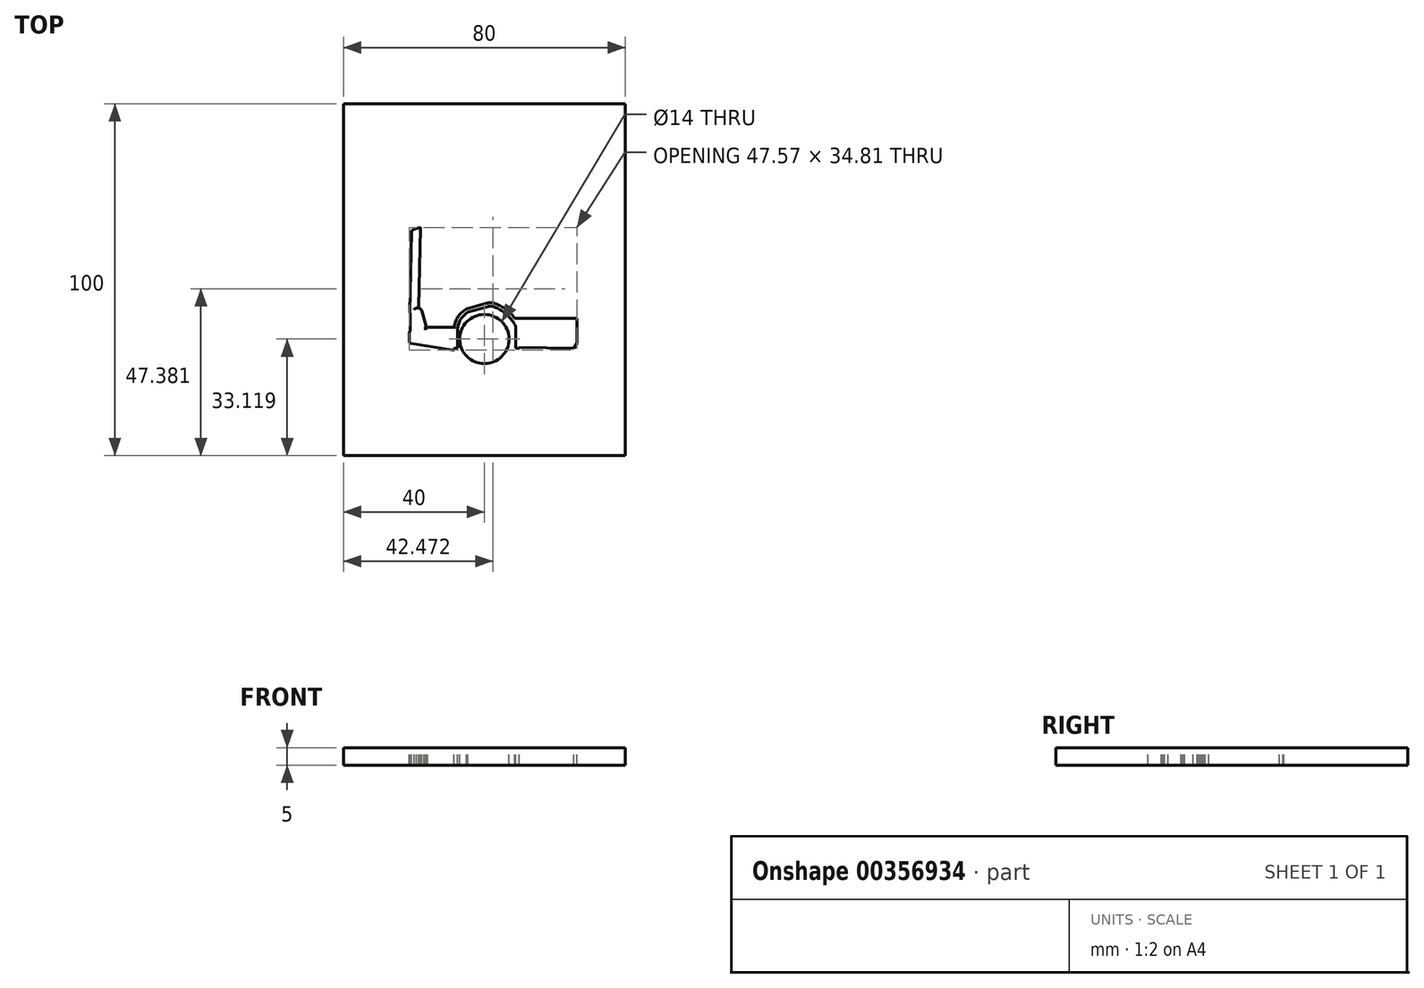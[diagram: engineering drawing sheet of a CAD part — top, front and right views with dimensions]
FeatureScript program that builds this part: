
annotation { "Feature Type Name" : "Feature", "Feature Type Description" : "" }
export const myFeature = defineFeature(function(context is Context, id is Id, definition is map)
    precondition{}
    {
        {
            var Q0;
            Q0=qCreatedBy(makeId("Top.planeOp"),FACE);
            var sketch = newSketch(context, id + "F0", { "sketchPlane" : qUnion([Q0])});
            skLineSegment(sketch, "E0.bottom", {"start": v(40, -50) * mm, "end": v(-40, -50) * mm});
            skLineSegment(sketch, "E0.top", {"start": v(40, 50) * mm, "end": v(-40, 50) * mm});
            skLineSegment(sketch, "E0.left", {"start": v(40, -50) * mm, "end": v(40, 50) * mm});
            skLineSegment(sketch, "E0.right", {"start": v(-40, -50) * mm, "end": v(-40, 50) * mm});
            skPoint(sketch, "E0.middle", {"position": v(0, 0) * mm});
            skCircle(sketch, "E1", {"center": v(0, -16.88) * mm, "radius": 7 * mm});
            skCircle(sketch, "E2", {"center": v(0, -16.88) * mm, "radius": 3.75 * mm});
            skCircle(sketch, "E3", {"center": v(0, -16.88) * mm, "radius": 1.5 * mm});
            skCircle(sketch, "E4", {"center": v(0, -16.88) * mm, "radius": 0.75 * mm});
            skLineSegment(sketch, "E5", {"start": v(-7.57, -19.52) * mm, "end": v(-7.57, -14.2) * mm});
            skArc(sketch, "E6", {"start": v(-7.57, -14.2) * mm, "mid": v(-6.8, -11.34) * mm, "end": v(-4.68, -9.26) * mm});
            skLineSegment(sketch, "E7", {"start": v(-4.68, -9.26) * mm, "end": v(0.98, -7.65) * mm});
            skArc(sketch, "E8", {"start": v(0.98, -7.65) * mm, "mid": v(1.86, -7.55) * mm, "end": v(2.72, -7.73) * mm});
            skPoint(sketch, "E9.end.orphan", {"position": v(7.1, -19.52) * mm});
            skArc(sketch, "E10", {"start": v(2.72, -7.73) * mm, "mid": v(6.11, -9.74) * mm, "end": v(8.64, -12.76) * mm});
            skPoint(sketch, "E11.end.orphan", {"position": v(7.3, -19.52) * mm});
            skArc(sketch, "E12", {"start": v(8.64, -12.76) * mm, "mid": v(8.84, -13.2) * mm, "end": v(8.94, -13.66) * mm});
            skLineSegment(sketch, "E13", {"start": v(8.94, -13.66) * mm, "end": v(8.94, -19.52) * mm});
            skLineSegment(sketch, "E14.0", {"start": v(9.94, -13.6) * mm, "end": v(9.94, -19.52) * mm});
            skArc(sketch, "E14.1", {"start": v(9.5, -12.25) * mm, "mid": v(9.8, -12.9) * mm, "end": v(9.94, -13.6) * mm});
            skArc(sketch, "E14.2", {"start": v(3.08, -6.8) * mm, "mid": v(6.76, -8.97) * mm, "end": v(9.5, -12.25) * mm});
            skLineSegment(sketch, "E14.3", {"start": v(-8.57, -19.52) * mm, "end": v(-8.57, -14.2) * mm});
            skArc(sketch, "E14.4", {"start": v(-8.57, -14.2) * mm, "mid": v(-7.63, -10.78) * mm, "end": v(-5.07, -8.33) * mm});
            skLineSegment(sketch, "E14.5", {"start": v(-5.07, -8.33) * mm, "end": v(0.7, -6.69) * mm});
            skArc(sketch, "E14.6", {"start": v(0.7, -6.69) * mm, "mid": v(1.9, -6.55) * mm, "end": v(3.08, -6.8) * mm});
            skLineSegment(sketch, "E15", {"start": v(-8.57, -19.52) * mm, "end": v(-7.57, -19.52) * mm});
            skLineSegment(sketch, "E16", {"start": v(8.94, -19.52) * mm, "end": v(9.94, -19.52) * mm});
            skLineSegment(sketch, "E17", {"start": v(9.94, -19.2) * mm, "end": v(25.47, -19.52) * mm});
            skLineSegment(sketch, "E18", {"start": v(25.47, -19.52) * mm, "end": v(26.26, -18.12) * mm});
            skLineSegment(sketch, "E19", {"start": v(26.26, -18.12) * mm, "end": v(9.94, -17.79) * mm});
            skLineSegment(sketch, "E20", {"start": v(26.26, -18.12) * mm, "end": v(26.26, -11.04) * mm});
            skLineSegment(sketch, "E21", {"start": v(26.26, -11.04) * mm, "end": v(8.7, -11.04) * mm});
            skLineSegment(sketch, "E22", {"start": v(9.94, -14.21) * mm, "end": v(26.26, -14.21) * mm});
            skLineSegment(sketch, "E23", {"start": v(11.31, -16.85) * mm, "end": v(11.35, -14.95) * mm});
            skLineSegment(sketch, "E24", {"start": v(11.35, -14.95) * mm, "end": v(15.33, -15.03) * mm});
            skLineSegment(sketch, "E25", {"start": v(15.33, -15.03) * mm, "end": v(15.33, -16.93) * mm});
            skLineSegment(sketch, "E26", {"start": v(15.33, -16.93) * mm, "end": v(11.31, -16.85) * mm});
            skPoint(sketch, "E27.orphan", {"position": v(11.31, -16.93) * mm});
            skLineSegment(sketch, "E28", {"start": v(-8.57, -19.52) * mm, "end": v(-8.57, -20.02) * mm});
            skLineSegment(sketch, "E29", {"start": v(-8.57, -20.02) * mm, "end": v(-8.84, -20.02) * mm});
            skLineSegment(sketch, "E30", {"start": v(-8.96, -20.01) * mm, "end": v(-20.9, -18.07) * mm});
            skLineSegment(sketch, "E31", {"start": v(-21.31, -17.58) * mm, "end": v(-21.31, -17.16) * mm});
            skPoint(sketch, "E32.visualSharp", {"position": v(-21.31, -18) * mm});
            skArc(sketch, "E32.filletArc", {"start": v(-21.31, -17.58) * mm, "mid": v(-21.2, -17.9) * mm, "end": v(-20.9, -18.07) * mm});
            skPoint(sketch, "E33.visualSharp", {"position": v(-8.9, -20.02) * mm});
            skArc(sketch, "E33.filletArc", {"start": v(-8.96, -20.01) * mm, "mid": v(-8.9, -20.02) * mm, "end": v(-8.84, -20.02) * mm});
            skLineSegment(sketch, "E34", {"start": v(-21.31, -17.16) * mm, "end": v(-15.78, -17.16) * mm});
            skLineSegment(sketch, "E35", {"start": v(-15.78, -17.16) * mm, "end": v(-15.37, -17.83) * mm});
            skLineSegment(sketch, "E36", {"start": v(-14.94, -18.07) * mm, "end": v(-8.57, -18.07) * mm});
            skPoint(sketch, "E37.visualSharp", {"position": v(-15.22, -18.07) * mm});
            skArc(sketch, "E37.filletArc", {"start": v(-15.37, -17.83) * mm, "mid": v(-15.18, -18) * mm, "end": v(-14.94, -18.07) * mm});
            skLineSegment(sketch, "E38", {"start": v(-21.31, -17.16) * mm, "end": v(-21.31, -15.3) * mm});
            skArc(sketch, "E39", {"start": v(-21.31, -15.3) * mm, "mid": v(-21.15, -14.65) * mm, "end": v(-20.69, -14.16) * mm});
            skLineSegment(sketch, "E40", {"start": v(-20.6, -14.13) * mm, "end": v(-17.1, -13.91) * mm});
            skLineSegment(sketch, "E41", {"start": v(-16.81, -13.9) * mm, "end": v(-15.78, -17.16) * mm});
            skLineSegment(sketch, "E42", {"start": v(-16.81, -13.9) * mm, "end": v(-8.57, -13.9) * mm});
            skLineSegment(sketch, "E43", {"start": v(-14.97, -13.5) * mm, "end": v(-8.57, -13.5) * mm});
            skLineSegment(sketch, "E44", {"start": v(-8.57, -13.5) * mm, "end": v(-8.57, -13.9) * mm});
            skLineSegment(sketch, "E45", {"start": v(-8.57, -17.7) * mm, "end": v(-14.97, -17.7) * mm});
            skPoint(sketch, "E46.end.orphan", {"position": v(-14.97, -18.07) * mm});
            skLineSegment(sketch, "E47", {"start": v(-14.97, -17.7) * mm, "end": v(-15.22, -17.7) * mm});
            skPoint(sketch, "E48.start.orphan", {"position": v(-14.97, -13.9) * mm});
            skLineSegment(sketch, "E49", {"start": v(-14.97, -13.5) * mm, "end": v(-15.22, -13.5) * mm});
            skLineSegment(sketch, "E50", {"start": v(-15.22, -17.7) * mm, "end": v(-16.11, -14.86) * mm});
            skArc(sketch, "E51", {"start": v(-16.11, -14.86) * mm, "mid": v(-16.09, -14.62) * mm, "end": v(-15.9, -14.48) * mm});
            skLineSegment(sketch, "E52", {"start": v(-15.9, -14.48) * mm, "end": v(-8.57, -14.2) * mm});
            skLineSegment(sketch, "E53", {"start": v(-8.57, -17.3) * mm, "end": v(-15.22, -17.3) * mm});
            skLineSegment(sketch, "E54", {"start": v(-15.22, -17.3) * mm, "end": v(-15.22, -17.7) * mm});
            skPoint(sketch, "E55.visualSharp", {"position": v(-20.64, -14.13) * mm});
            skArc(sketch, "E55.filletArc", {"start": v(-20.6, -14.13) * mm, "mid": v(-20.64, -14.14) * mm, "end": v(-20.69, -14.16) * mm});
            skLineSegment(sketch, "E56", {"start": v(-21.03, -14.46) * mm, "end": v(-21.03, -9.77) * mm});
            skArc(sketch, "E57", {"start": v(-21.03, -9.77) * mm, "mid": v(-20.93, -9.4) * mm, "end": v(-20.66, -9.12) * mm});
            skArc(sketch, "E58", {"start": v(-20.66, -9.12) * mm, "mid": v(-19.78, -8.74) * mm, "end": v(-18.85, -8.55) * mm});
            skArc(sketch, "E59", {"start": v(-18.85, -8.55) * mm, "mid": v(-18.5, -8.66) * mm, "end": v(-18.32, -8.98) * mm});
            skLineSegment(sketch, "E60", {"start": v(-18.32, -8.98) * mm, "end": v(-17.13, -13) * mm});
            skArc(sketch, "E61", {"start": v(-17.13, -13) * mm, "mid": v(-17.16, -13.32) * mm, "end": v(-17.4, -13.53) * mm});
            skLineSegment(sketch, "E62", {"start": v(-17.4, -13.53) * mm, "end": v(-20.6, -13.73) * mm});
            skArc(sketch, "E63", {"start": v(-20.6, -13.73) * mm, "mid": v(-20.85, -13.81) * mm, "end": v(-21.03, -14.01) * mm});
            skArc(sketch, "E64.0", {"start": v(-18.89, -8.05) * mm, "mid": v(-18.18, -8.27) * mm, "end": v(-17.83, -8.92) * mm});
            skArc(sketch, "E65.0", {"start": v(-16.65, -12.86) * mm, "mid": v(-16.66, -13.42) * mm, "end": v(-17, -13.87) * mm});
            skLineSegment(sketch, "E65.1", {"start": v(-17.84, -8.84) * mm, "end": v(-16.65, -12.86) * mm});
            skArc(sketch, "E66.filletArc", {"start": v(-17.1, -13.91) * mm, "mid": v(-17.05, -13.9) * mm, "end": v(-17, -13.87) * mm});
            skLineSegment(sketch, "E67", {"start": v(-16.81, -13.9) * mm, "end": v(-17.1, -13.91) * mm});
            skArc(sketch, "E68", {"start": v(-18.89, -8.05) * mm, "mid": v(-20.08, -8.46) * mm, "end": v(-20.93, -9.4) * mm});
            skLineSegment(sketch, "E69.0", {"start": v(-17.35, -8.76) * mm, "end": v(-16.76, -10.74) * mm});
            skLineSegment(sketch, "E70", {"start": v(-16.76, -10.74) * mm, "end": v(-7.89, -10.74) * mm});
            skArc(sketch, "E71.0", {"start": v(-16.16, -13.5) * mm, "mid": v(-16.24, -13.7) * mm, "end": v(-16.34, -13.9) * mm});
            skArc(sketch, "E72.trimOffspring", {"start": v(-16.7, -14.27) * mm, "mid": v(-16.7, -14.27) * mm, "end": v(-16.7, -14.28) * mm});
            skPoint(sketch, "E73.end.orphan", {"position": v(-15.22, -13.9) * mm});
            skLineSegment(sketch, "E74", {"start": v(-15.22, -13.5) * mm, "end": v(-16.16, -13.5) * mm});
            skPoint(sketch, "E75.orphan", {"position": v(-16.17, -12.72) * mm});
            skPoint(sketch, "E76.end.orphan", {"position": v(-19.85, -8.05) * mm});
            skArc(sketch, "E77", {"start": v(-17.35, -8.76) * mm, "mid": v(-17.94, -8.01) * mm, "end": v(-18.89, -7.9) * mm});
            skArc(sketch, "E78", {"start": v(-18.89, -7.9) * mm, "mid": v(-19.93, -8.37) * mm, "end": v(-20.77, -9.13) * mm});
            skLineSegment(sketch, "E79", {"start": v(-21.03, -12.91) * mm, "end": v(-19.3, -12.46) * mm});
            skLineSegment(sketch, "E80", {"start": v(-18.96, -11.84) * mm, "end": v(-19.47, -9.92) * mm});
            skLineSegment(sketch, "E81", {"start": v(-20.08, -9.56) * mm, "end": v(-21.03, -9.81) * mm});
            skPoint(sketch, "E82.visualSharp", {"position": v(-19.6, -9.43) * mm});
            skArc(sketch, "E82.filletArc", {"start": v(-19.47, -9.92) * mm, "mid": v(-19.7, -9.61) * mm, "end": v(-20.08, -9.56) * mm});
            skPoint(sketch, "E83.visualSharp", {"position": v(-18.83, -12.33) * mm});
            skArc(sketch, "E83.filletArc", {"start": v(-19.3, -12.46) * mm, "mid": v(-19, -12.22) * mm, "end": v(-18.96, -11.84) * mm});
            skLineSegment(sketch, "E84", {"start": v(-21.03, -9.77) * mm, "end": v(-21.2, -9.24) * mm});
            skPoint(sketch, "E85.end.orphan", {"position": v(-19.41, 13.52) * mm});
            skPoint(sketch, "E85.start.orphan", {"position": v(-19.41, 13.69) * mm});
            skLineSegment(sketch, "E86", {"start": v(-21.2, -9.24) * mm, "end": v(-20.65, 13.46) * mm});
            skArc(sketch, "E87", {"start": v(-20.65, 13.46) * mm, "mid": v(-20.57, 13.75) * mm, "end": v(-20.36, 13.96) * mm});
            skArc(sketch, "E88", {"start": v(-20.36, 13.96) * mm, "mid": v(-19.85, 14.2) * mm, "end": v(-19.31, 14.38) * mm});
            skLineSegment(sketch, "E89", {"start": v(-19.31, 14.38) * mm, "end": v(-18.1, 14.68) * mm});
            skLineSegment(sketch, "E90", {"start": v(-18.1, 14.68) * mm, "end": v(-18.64, -7.86) * mm});
            skPoint(sketch, "E91.orphan", {"position": v(-18.64, -7.9) * mm});
            skLineSegment(sketch, "E92", {"start": v(-20.65, 13.46) * mm, "end": v(-20.65, 13.75) * mm});
            skArc(sketch, "E93", {"start": v(-20.65, 13.75) * mm, "mid": v(-20.61, 13.91) * mm, "end": v(-20.5, 14.03) * mm});
            skArc(sketch, "E94", {"start": v(-20.5, 14.03) * mm, "mid": v(-19.94, 14.32) * mm, "end": v(-19.33, 14.51) * mm});
            skLineSegment(sketch, "E95", {"start": v(-19.33, 14.51) * mm, "end": v(-18.22, 14.78) * mm});
            skArc(sketch, "E96", {"start": v(-18.22, 14.78) * mm, "mid": v(-18.13, 14.76) * mm, "end": v(-18.1, 14.68) * mm});
            skSolve(sketch);
        }
        {
            var Q0;
            Q0=makeQuery(id+"F0.imprint","IMPRINT",FACE,{"disambiguationData":[TD([[makeQuery(id+"F0.imprint","IMPRINT",EDGE,{"derivedFrom":sQuery(id+"F0.wireOp",EDGE,"E0.bottom")}),-1.0]])]});
            extrude(context, id + "F1", {"entities" : qUnion([Q0]), "oppositeDirection" : true, "depth" : 5 * mm});
        }
    });
